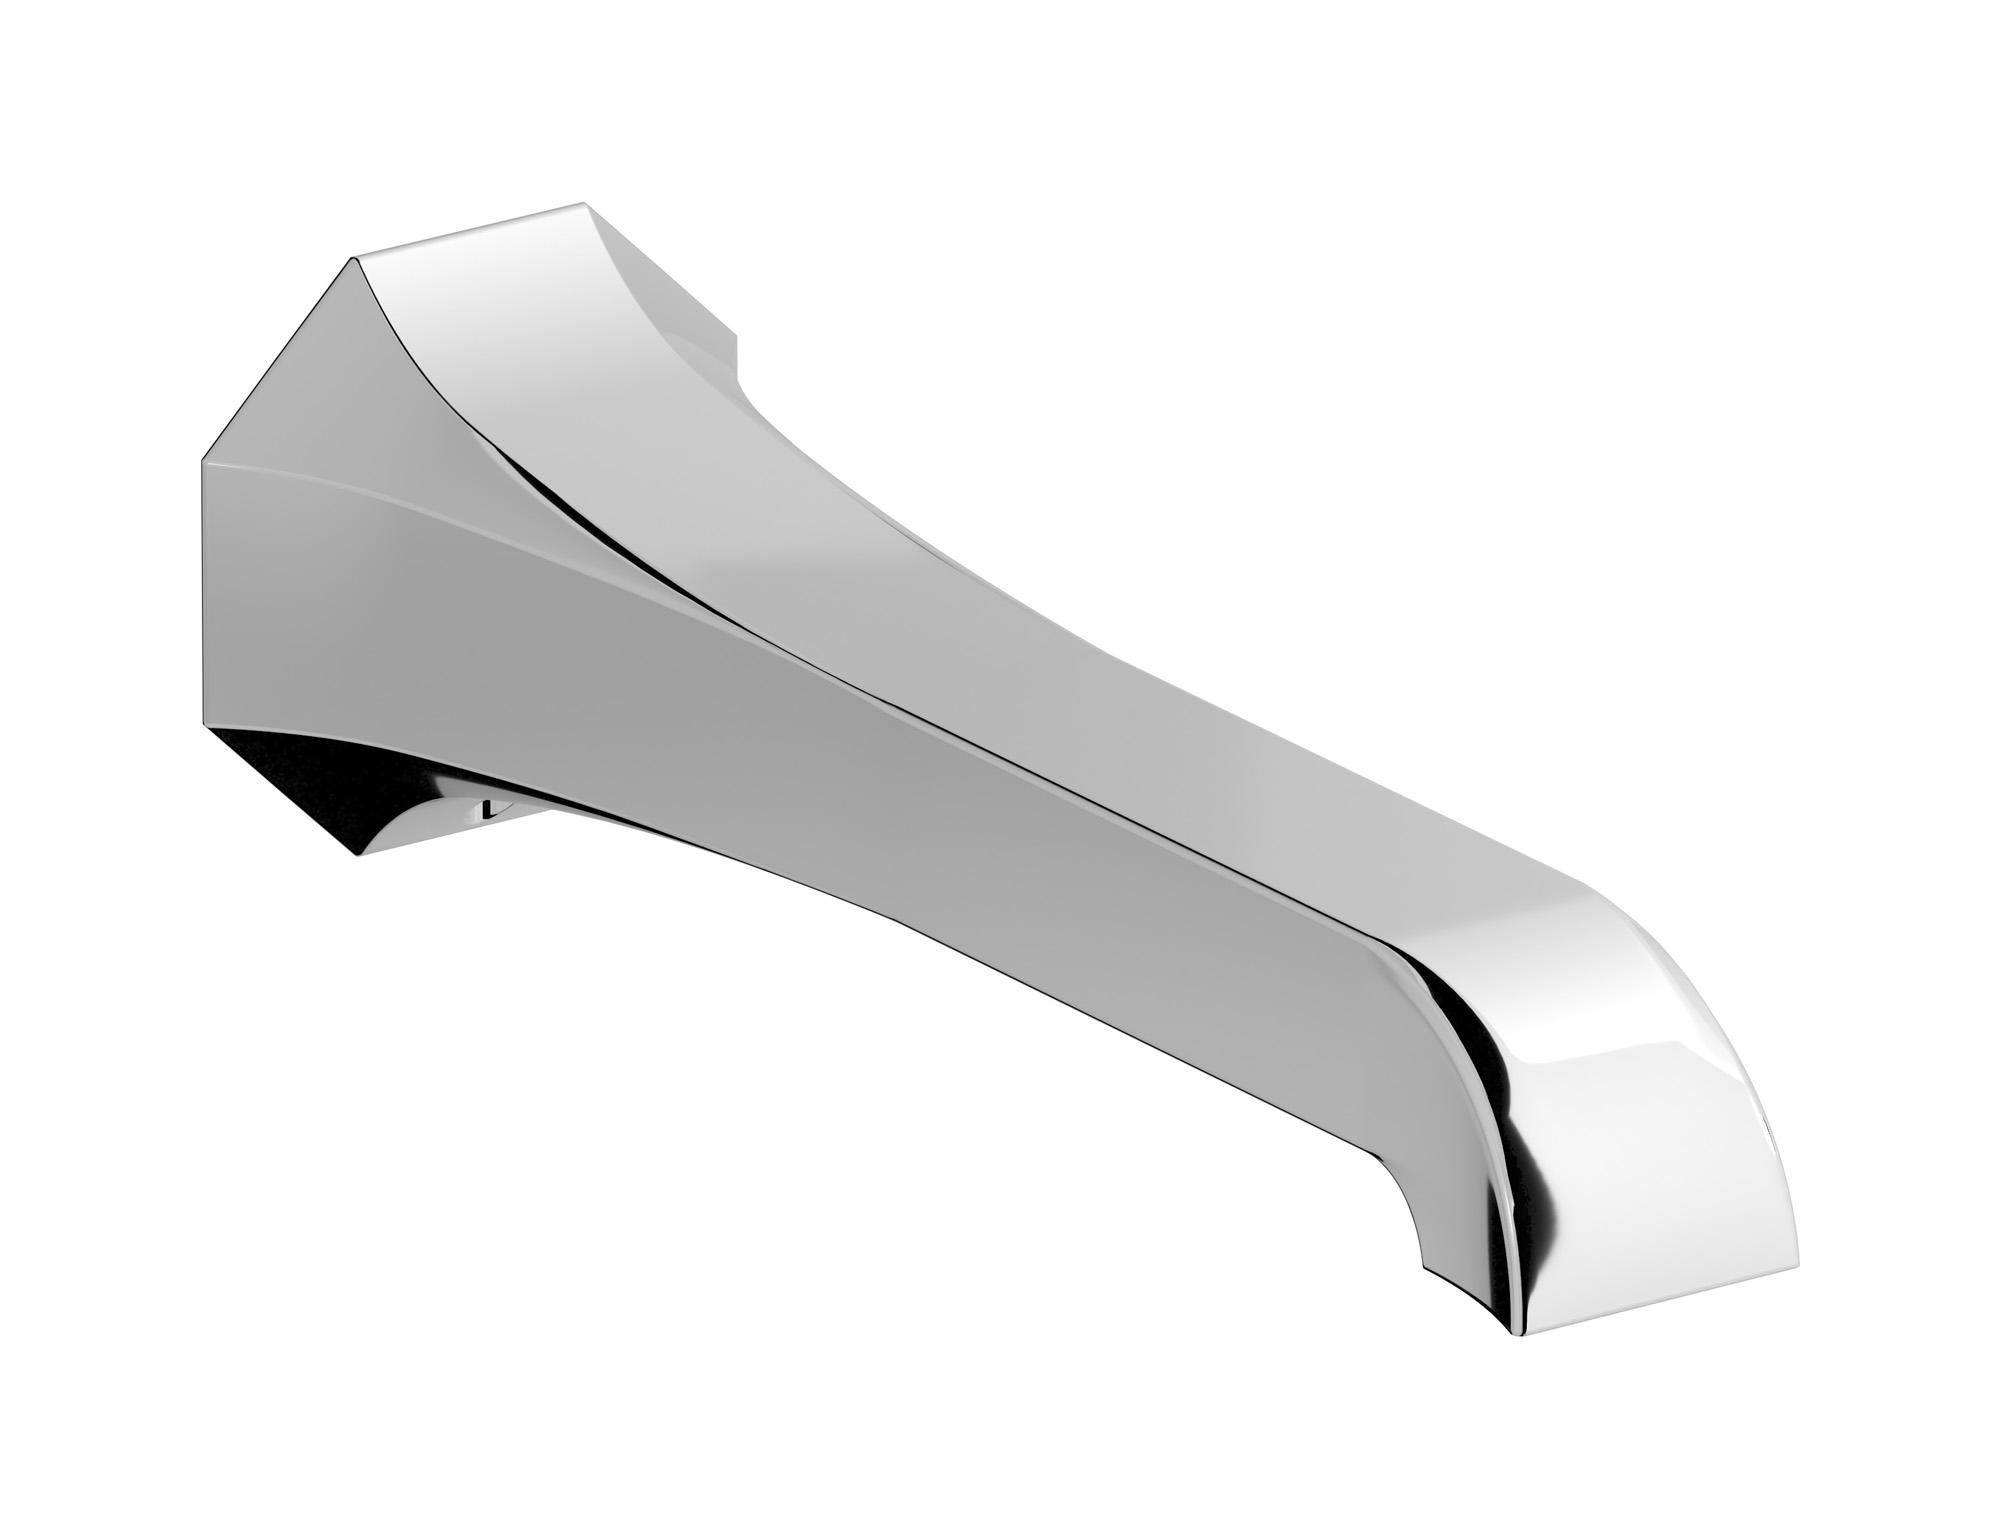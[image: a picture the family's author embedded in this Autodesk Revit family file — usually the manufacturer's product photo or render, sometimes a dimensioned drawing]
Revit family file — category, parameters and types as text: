
# Revit family: BT327
name_source: partatom
category: Apparecchi idraulici
units: mm (PartAtom-declared; Revit-internal decimal feet)

## family parameters
Basato su piano di lavoro = No
Condiviso = No
Mantieni orientamento annotazione = No
Numero OmniClass = 23.45.55.17
Punto di calcolo locali = No
Quota connettore circolare = Usa diametro
Sempre verticale = Sì
Taglio con vuoti quando caricato = No
Tipo di parte = Normale
Titolo OmniClass = Mixing Faucets

## types (7) — shared parameters
Commenti sul tipo = Wall mounted spout
Connessione CW = No
Connessione HW = No
Connessione di scarico = No
Connessione di ventilazione = No
Descrizione = Wall mounted spout
Produttore = IB Rubinetterie S.p.A.
URL = https://www.weareib.it
Water inlet = 10 mm  [stored 0.0328084 ft]
zero-valued in all types: Prospetto di default

## per-type parameters (varying)
| type | Finishes surface | Immagine tipo | Modello |
| Chrome | IB_Chrome | BT327CC.jpg | BT327CC |
| Pale Gold | IB_Pale gold | BT327II.jpg | BT327II |
| Modern Bronze | IB_Modern bronze | BT327MB.jpg | BT327MB |
| Gold | IB_gold | BT327OO.jpg | BT327OO |
| Platinum | IB_Platinum | BT327PL.jpg | BT327PL |
| Rose Gold | IB_Rose gold | BT327RS.jpg | BT327RS |
| Brushed Nickel | IB_Brushed nickel | BT327SS.jpg | BT327SS |

note: [stored X ft] marks values corroborated as IEEE doubles in the binary element streams (Revit-internal decimal feet)
